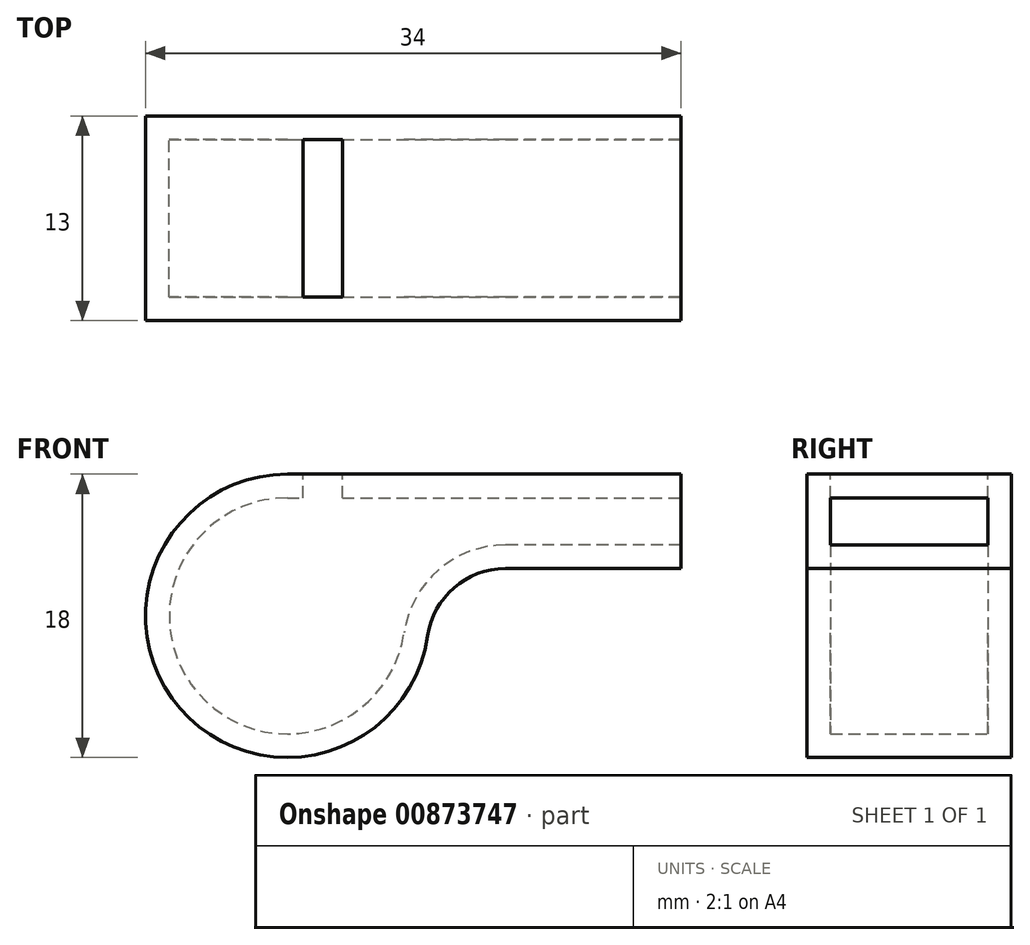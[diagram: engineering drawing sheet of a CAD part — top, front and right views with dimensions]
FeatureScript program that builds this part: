
annotation { "Feature Type Name" : "Feature", "Feature Type Description" : "" }
export const myFeature = defineFeature(function(context is Context, id is Id, definition is map)
    precondition{}
    {
        {
            var Q0;
            Q0=qCreatedBy(makeId("Front.planeOp"),FACE);
            var sketch = newSketch(context, id + "F0", { "sketchPlane" : qUnion([Q0])});
            skArc(sketch, "E0", {"start": v(0, 9) * mm, "mid": v(-6.8, -5.9) * mm, "end": v(8.9, -1.29) * mm});
            skLineSegment(sketch, "E1", {"start": v(0, 9) * mm, "end": v(25, 9) * mm});
            skLineSegment(sketch, "E2", {"start": v(25, 9) * mm, "end": v(25, 3) * mm});
            skLineSegment(sketch, "E3", {"start": v(25, 3) * mm, "end": v(13.86, 3) * mm});
            skPoint(sketch, "E4.visualSharp", {"position": v(8.49, 3) * mm});
            skArc(sketch, "E4.filletArc", {"start": v(13.86, 3) * mm, "mid": v(10.58, 1.78) * mm, "end": v(8.9, -1.29) * mm});
            skSolve(sketch);
        }
        {
            var Q0;
            Q0=makeQuery(id+"F0.imprint","IMPRINT",FACE,{"disambiguationData":[TD([[makeQuery(id+"F0.imprint","IMPRINT",EDGE,{"derivedFrom":sQuery(id+"F0.wireOp",EDGE,"E0")}),1.0]])]});
            extrude(context, id + "F1", {"entities" : qUnion([Q0]), "endBound" : BoundingType.SYMMETRIC, "depth" : 13 * mm, "offsetDistance" : 25 * mm});
        }
        {
            var Q0;
            Q0=makeQuery(id+"F1.opExtrude","SWEPT_FACE",FACE,{"disambiguationData":[OSD([sQuery(id+"F0.wireOp",EDGE,"E2")])]});
            shell(context, id + "F2", {"entities" : qUnion([Q0]), "thickness" : 1.5 * mm});
        }
        {
            var Q0;
            Q0=makeQuery(id+"F1.opExtrude","SWEPT_FACE",FACE,{"disambiguationData":[OSD([sQuery(id+"F0.wireOp",EDGE,"E1")])]});
            var sketch = newSketch(context, id + "F3", { "sketchPlane" : qUnion([Q0])});
            skLineSegment(sketch, "E5.bottom", {"start": v(1, 5) * mm, "end": v(3.5, 5) * mm});
            skLineSegment(sketch, "E5.top", {"start": v(1, -5) * mm, "end": v(3.5, -5) * mm});
            skLineSegment(sketch, "E5.left", {"start": v(1, 5) * mm, "end": v(1, -5) * mm});
            skLineSegment(sketch, "E5.right", {"start": v(3.5, 5) * mm, "end": v(3.5, -5) * mm});
            skSolve(sketch);
        }
        {
            var Q0;
            Q0=makeQuery(id+"F3.imprint","IMPRINT",FACE,{"disambiguationData":[TD([[makeQuery(id+"F3.imprint","IMPRINT",EDGE,{"derivedFrom":sQuery(id+"F3.wireOp",EDGE,"E5.bottom")}),-1.0]])]});
            extrude(context, id + "F4", {"entities" : qUnion([Q0]), "operationType" : NewBodyOperationType.REMOVE, "oppositeDirection" : true, "depth" : 1.5 * mm, "offsetDistance" : 25 * mm});
        }
    });
